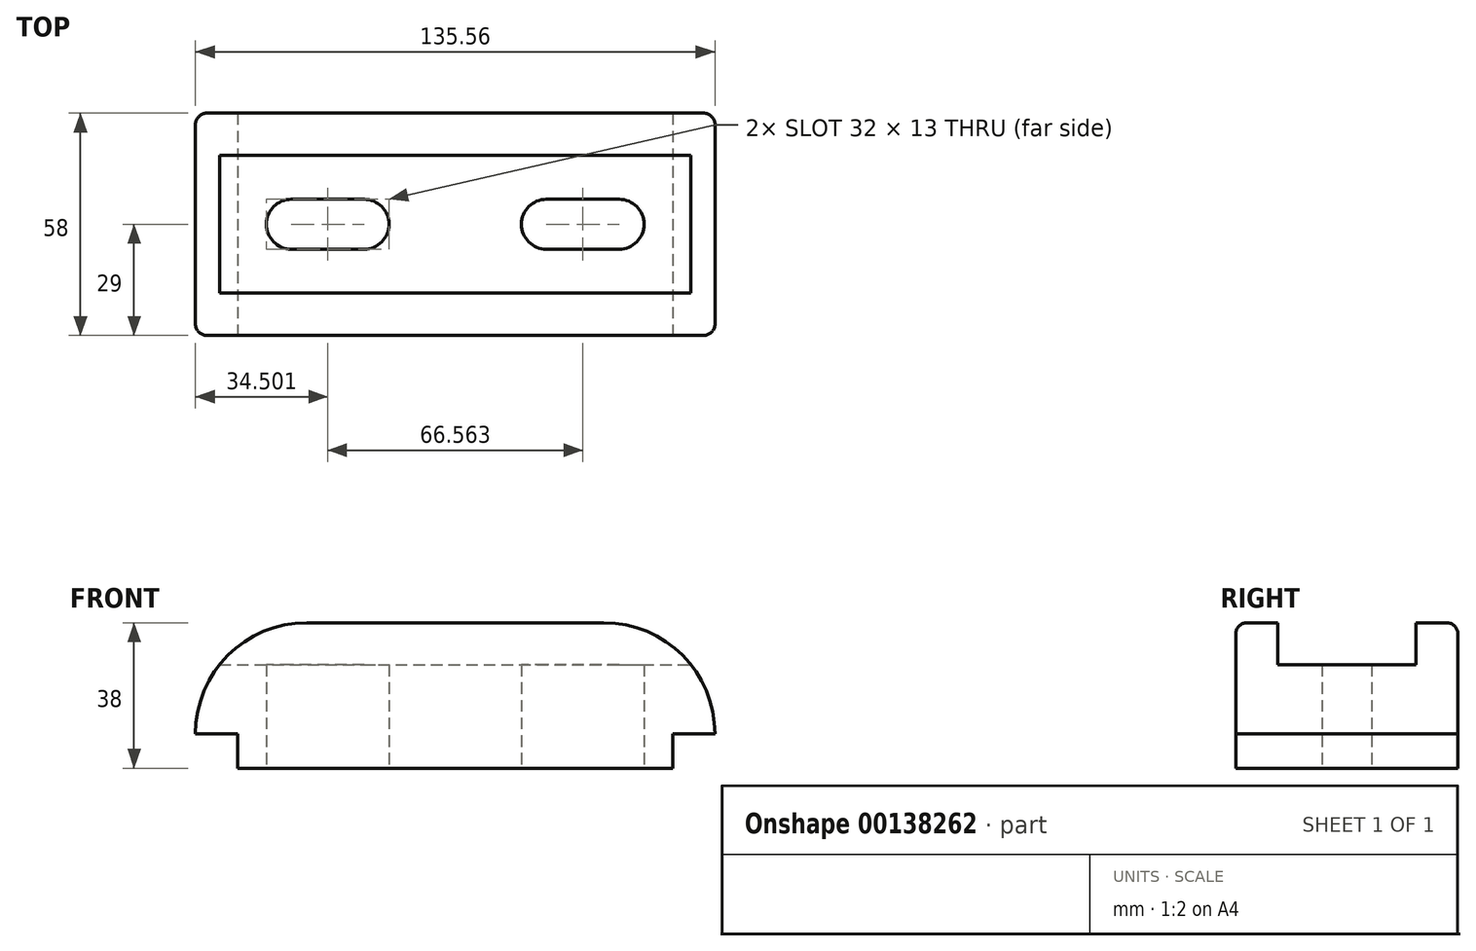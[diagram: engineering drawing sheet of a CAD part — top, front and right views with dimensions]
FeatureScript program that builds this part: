
annotation { "Feature Type Name" : "Feature", "Feature Type Description" : "" }
export const myFeature = defineFeature(function(context is Context, id is Id, definition is map)
    precondition{}
    {
        {
            var Q0;
            Q0=qCreatedBy(makeId("Front.planeOp"),FACE);
            var sketch = newSketch(context, id + "F0", { "sketchPlane" : qUnion([Q0])});
            skLineSegment(sketch, "E0", {"start": v(-49.46, 0) * mm, "end": v(55.54, 0) * mm});
            skLineSegment(sketch, "E1", {"start": v(-49.46, 0) * mm, "end": v(-49.46, 9) * mm});
            skLineSegment(sketch, "E2", {"start": v(-49.46, 9) * mm, "end": v(-69.02, 9) * mm});
            skLineSegment(sketch, "E3", {"start": v(55.54, 0) * mm, "end": v(55.54, 9) * mm});
            skLineSegment(sketch, "E4", {"start": v(55.54, 9) * mm, "end": v(66.54, 9) * mm});
            skLineSegment(sketch, "E5", {"start": v(66.54, 9) * mm, "end": v(66.54, 38) * mm});
            skLineSegment(sketch, "E6", {"start": v(-69.02, 9) * mm, "end": v(-40.02, 9) * mm});
            skArc(sketch, "E7", {"start": v(-40.02, 38) * mm, "mid": v(-60.53, 29.5) * mm, "end": v(-69.02, 9) * mm});
            skLineSegment(sketch, "E8", {"start": v(55.54, 9) * mm, "end": v(38.68, 9) * mm});
            skLineSegment(sketch, "E9", {"start": v(66.54, 9) * mm, "end": v(37.54, 9) * mm});
            skArc(sketch, "E10", {"start": v(66.54, 9) * mm, "mid": v(58.05, 29.5) * mm, "end": v(37.54, 38) * mm});
            skLineSegment(sketch, "E11", {"start": v(-40.02, 38) * mm, "end": v(37.54, 38) * mm});
            skLineSegment(sketch, "E12", {"start": v(-58.02, 0) * mm, "end": v(-58.02, 9) * mm});
            skLineSegment(sketch, "E13", {"start": v(-58.02, 0) * mm, "end": v(-49.46, 0) * mm});
            skSolve(sketch);
        }
        {
            var Q0;
            Q0 = qSketchRegion(id + "F0", true);
            extrude(context, id + "F1", {"entities" : qUnion([Q0]), "oppositeDirection" : true, "depth" : 58 * mm});
        }
        {
            var Q0;
            Q0=makeQuery(id+"F1.opExtrude","SWEPT_FACE",FACE,{"disambiguationData":[OSD([sQuery(id+"F0.wireOp",EDGE,"E11")])]});
            var sketch = newSketch(context, id + "F2", { "sketchPlane" : qUnion([Q0])});
            skLineSegment(sketch, "E14", {"start": v(0, 58) * mm, "end": v(0, 47) * mm});
            skPoint(sketch, "E14.startSnap0", {"position": v(-1.24, 58) * mm});
            skLineSegment(sketch, "E15", {"start": v(0, 0) * mm, "end": v(0, 11) * mm});
            skLineSegment(sketch, "E16", {"start": v(0, 11) * mm, "end": v(-64.2, 11) * mm});
            skLineSegment(sketch, "E17", {"start": v(-64.2, 11) * mm, "end": v(-64.2, 47) * mm});
            skLineSegment(sketch, "E18", {"start": v(-64.2, 47) * mm, "end": v(60.26, 47) * mm});
            skLineSegment(sketch, "E19", {"start": v(60.26, 11) * mm, "end": v(0, 11) * mm});
            skLineSegment(sketch, "E20", {"start": v(60.26, 47) * mm, "end": v(64.4, 47) * mm});
            skLineSegment(sketch, "E21", {"start": v(64.4, 47) * mm, "end": v(64.4, 11) * mm});
            skLineSegment(sketch, "E22", {"start": v(64.4, 11) * mm, "end": v(60.26, 11) * mm});
            skSolve(sketch);
        }
        {
            var Q0;
            Q0 = qSketchRegion(id + "F2", true);
            extrude(context, id + "F3", {"entities" : qUnion([Q0]), "operationType" : NewBodyOperationType.REMOVE, "oppositeDirection" : true, "depth" : 11 * mm});
        }
        {
            var Q0;
            Q0=makeQuery(id+"F1.opExtrude","CAP_EDGE",EDGE,{"disambiguationData":[OSD([sQuery(id+"F0.wireOp",EDGE,"E11")])],"isStart":true});
            var Q1;
            Q1=makeQuery(id+"F1.opExtrude","CAP_EDGE",EDGE,{"disambiguationData":[OSD([sQuery(id+"F0.wireOp",EDGE,"E11")])],"isStart":false});
            var Q2;
            Q2=makeQuery(id+"F1.opExtrude","CAP_EDGE",EDGE,{"disambiguationData":[OSD([sQuery(id+"F0.wireOp",EDGE,"E7")])],"isStart":true});
            var Q3;
            Q3=makeQuery(id+"F1.opExtrude","CAP_EDGE",EDGE,{"disambiguationData":[OSD([sQuery(id+"F0.wireOp",EDGE,"E10")])],"isStart":true});
            var Q4;
            Q4=makeQuery(id+"F1.opExtrude","CAP_EDGE",EDGE,{"disambiguationData":[OSD([sQuery(id+"F0.wireOp",EDGE,"E7")])],"isStart":false});
            var Q5;
            Q5=makeQuery(id+"F1.opExtrude","CAP_EDGE",EDGE,{"disambiguationData":[OSD([sQuery(id+"F0.wireOp",EDGE,"E10")])],"isStart":false});
            fillet(context, id + "F4", {"entities" : qUnion([Q0, Q1, Q2, Q3, Q4, Q5]), "radius" : 3 * mm, "allowEdgeOverflow" : false});
        }
        {
            var Q0;
            Q0=makeQuery(id+"F1.opExtrude","SWEPT_FACE",FACE,{"disambiguationData":[OSD([sQuery(id+"F0.wireOp",EDGE,"E0"),sQuery(id+"F0.wireOp",EDGE,"E13")])]});
            var sketch = newSketch(context, id + "F5", { "sketchPlane" : qUnion([Q0])});
            skLineSegment(sketch, "E23", {"start": v(-58.02, -29) * mm, "end": v(-44.02, -29) * mm});
            skLineSegment(sketch, "E24", {"start": v(-44.02, -29) * mm, "end": v(-25.02, -29) * mm});
            skLineSegment(sketch, "E25", {"start": v(55.54, -29) * mm, "end": v(41.54, -29) * mm});
            skLineSegment(sketch, "E26", {"start": v(41.54, -29) * mm, "end": v(22.54, -29) * mm});
            skArc(sketch, "E27", {"start": v(-44.02, -22.5) * mm, "mid": v(-50.52, -29) * mm, "end": v(-44.02, -35.5) * mm});
            skArc(sketch, "E28", {"start": v(-25.02, -35.5) * mm, "mid": v(-18.52, -29) * mm, "end": v(-25.02, -22.5) * mm});
            skArc(sketch, "E29", {"start": v(22.54, -22.5) * mm, "mid": v(16.04, -29) * mm, "end": v(22.54, -35.5) * mm});
            skArc(sketch, "E30", {"start": v(41.54, -35.5) * mm, "mid": v(48.04, -29) * mm, "end": v(41.54, -22.5) * mm});
            skLineSegment(sketch, "E31", {"start": v(-44.02, -22.5) * mm, "end": v(-25.02, -22.5) * mm});
            skLineSegment(sketch, "E32", {"start": v(-44.02, -35.5) * mm, "end": v(-25.02, -35.5) * mm});
            skLineSegment(sketch, "E33", {"start": v(22.54, -22.5) * mm, "end": v(41.54, -22.5) * mm});
            skLineSegment(sketch, "E34", {"start": v(22.54, -35.5) * mm, "end": v(41.54, -35.5) * mm});
            skSolve(sketch);
        }
        {
            var Q0;
            Q0 = qSketchRegion(id + "F5", true);
            extrude(context, id + "F6", {"entities" : qUnion([Q0]), "operationType" : NewBodyOperationType.REMOVE, "endBound" : BoundingType.THROUGH_ALL, "oppositeDirection" : true, "depth" : 25 * mm});
        }
    });
